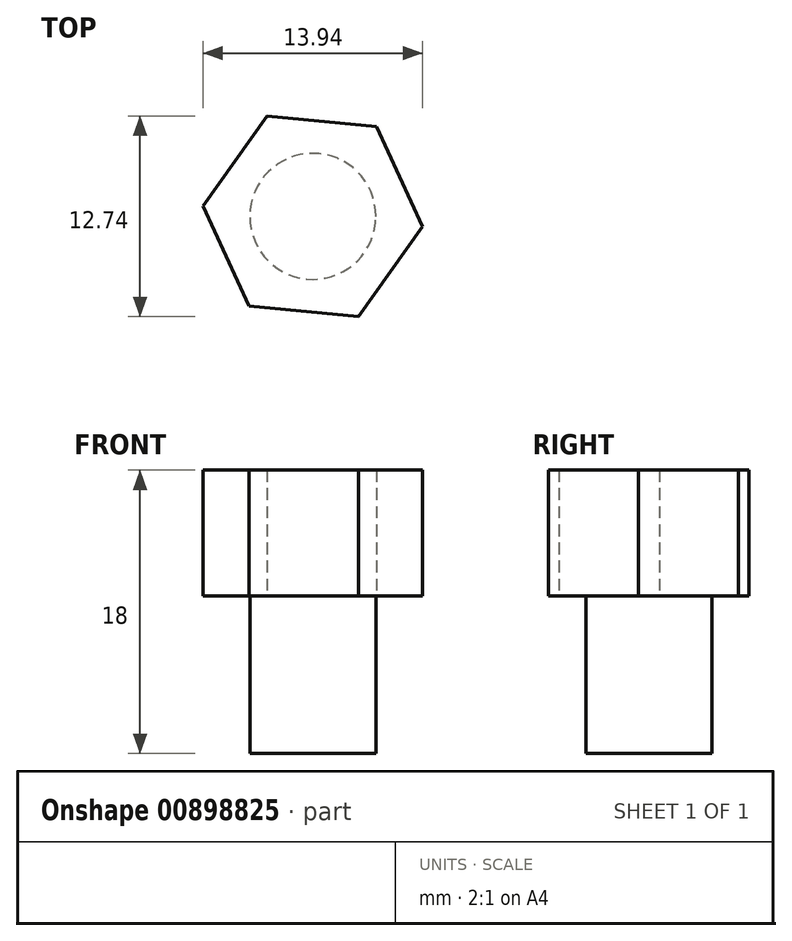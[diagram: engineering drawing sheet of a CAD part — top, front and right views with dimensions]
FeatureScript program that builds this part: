
annotation { "Feature Type Name" : "Feature", "Feature Type Description" : "" }
export const myFeature = defineFeature(function(context is Context, id is Id, definition is map)
    precondition{}
    {
        {
            var Q0;
            Q0=qCreatedBy(makeId("Front.planeOp"),FACE);
            var sketch = newSketch(context, id + "F0", { "sketchPlane" : qUnion([Q0])});
            skLineSegment(sketch, "E0", {"start": v(4, 90) * mm, "end": v(0, 90) * mm});
            skLineSegment(sketch, "E1", {"start": v(0, 90) * mm, "end": v(0, 65) * mm});
            skLineSegment(sketch, "E2", {"start": v(0, 65) * mm, "end": v(0, 0) * mm});
            skLineSegment(sketch, "E3", {"start": v(0, 0) * mm, "end": v(4, 0) * mm});
            skLineSegment(sketch, "E4", {"start": v(4, 0) * mm, "end": v(4, 90) * mm});
            skSolve(sketch);
        }
        {
            var Q0;
            Q0=qSketchRegion(id+"F0",true);
            var Q1;
            Q1=sQuery(id+"F0.wireOp",EDGE,"E2");
            revolve(context, id + "F1", {"surfaceOperationType" : NewSurfaceOperationType.NEW, "entities" : qUnion([Q0]), "axis" : qUnion([Q1]), "revolveType" : RevolveType.FULL});
        }
        {
            var Q0;
            Q0=makeQuery(id+"F1.opRevolve","SWEPT_FACE",FACE,{"disambiguationData":[OSD([sQuery(id+"F0.wireOp",EDGE,"E0")])]});
            var sketch = newSketch(context, id + "F2", { "sketchPlane" : qUnion([Q0])});
            skLineSegment(sketch, "E5.0", {"start": v(4.06, 5.7) * mm, "end": v(6.97, -0.66) * mm});
            skLineSegment(sketch, "E5.1", {"start": v(6.97, -0.66) * mm, "end": v(2.9, -6.37) * mm});
            skLineSegment(sketch, "E5.2", {"start": v(2.9, -6.37) * mm, "end": v(-4.06, -5.7) * mm});
            skLineSegment(sketch, "E5.3", {"start": v(-4.06, -5.7) * mm, "end": v(-6.97, 0.66) * mm});
            skLineSegment(sketch, "E5.4", {"start": v(-6.97, 0.66) * mm, "end": v(-2.9, 6.37) * mm});
            skLineSegment(sketch, "E5.5", {"start": v(-2.9, 6.37) * mm, "end": v(4.06, 5.7) * mm});
            skSolve(sketch);
        }
        {
            var Q0;
            Q0=qSketchRegion(id+"F2",true);
            extrude(context, id + "F3", {"entities" : qUnion([Q0]), "operationType" : NewBodyOperationType.ADD, "depth" : 8 * mm, "offsetDistance" : 25 * mm});
        }
        {
            var Q0;
            Q0=qCreatedBy(makeId("Front.planeOp"),FACE);
            var sketch = newSketch(context, id + "F4", { "sketchPlane" : qUnion([Q0])});
            skLineSegment(sketch, "E6", {"start": v(0, 0) * mm, "end": v(5, 0) * mm});
            skLineSegment(sketch, "E7", {"start": v(5, 0) * mm, "end": v(5, 80) * mm});
            skLineSegment(sketch, "E8", {"start": v(5, 80) * mm, "end": v(0, 80) * mm});
            skLineSegment(sketch, "E9", {"start": v(0, 80) * mm, "end": v(0, 0) * mm});
            skSolve(sketch);
        }
        {
            var Q0;
            Q0 = qSketchRegion(id + "F4", true);
            var Q1;
            Q1=sQuery(id+"F4.wireOp",EDGE,"E9");
            revolve(context, id + "F5", {"operationType" : NewBodyOperationType.REMOVE, "surfaceOperationType" : NewSurfaceOperationType.NEW, "entities" : qUnion([Q0]), "axis" : qUnion([Q1]), "revolveType" : RevolveType.FULL, "oppositeDirection" : true});
        }
    });
